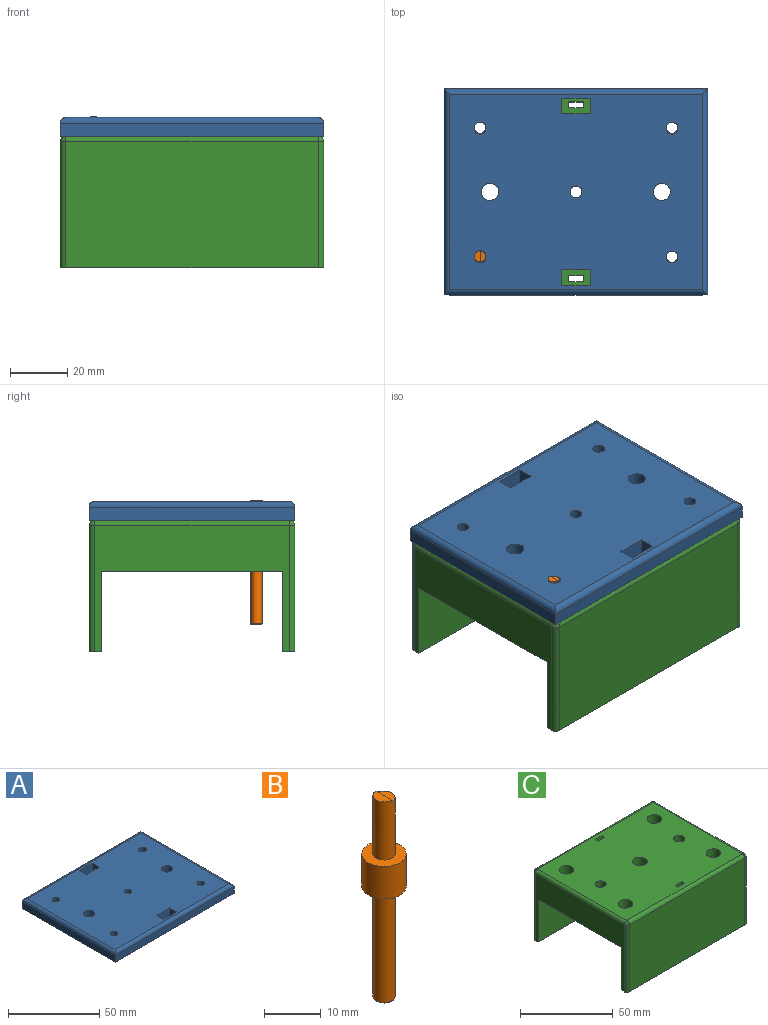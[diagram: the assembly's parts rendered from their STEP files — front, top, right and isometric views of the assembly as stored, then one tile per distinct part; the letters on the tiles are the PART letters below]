
ASSEMBLY  parts=3 mates=3
PART A: 35 faces, bbox 92x71.9x10.5 mm
  f0: plane 88x67.9mm, normal (0,0,1), area 5741mm2, adj f16,f17,f18,f19,f20,f21,f22,f23
  f1: plane 92x71.9mm, normal (0,0,-1), area 6201.9mm2, adj f2,f3,f4,f5,f6,f8,f10,f12
  f2: plane 71.9x4.5mm, normal (1,0,0), area 323.6mm2, adj f1,f3,f5,f21
  f3: plane 92x4.5mm, normal (0,1,0), area 414mm2, adj f1,f2,f4,f22
  f4: plane 71.9x4.5mm, normal (-1,0,0), area 323.6mm2, adj f1,f3,f5,f24
  f5: plane 92x4.5mm, normal (0,-1,0), area 414mm2, adj f1,f2,f4,f23
  f6: cylinder r=3.96mm len=7.92mm, axis (0,0,1), area 99.5mm2, adj f1,f7
  f7: plane 7.92x7.92mm, normal (0,0,-1), area 35.7mm2, adj f6,f20
  f8: cylinder r=3.96mm len=7.92mm, axis (0,0,1), area 99.5mm2, adj f1,f9
  f9: plane 7.92x7.92mm, normal (0,0,-1), area 35.7mm2, adj f8,f19
  f10: cylinder r=3.96mm len=7.92mm, axis (0,0,1), area 99.5mm2, adj f1,f11
  f11: plane 7.92x7.92mm, normal (0,0,-1), area 35.7mm2, adj f10,f18
  f12: cylinder r=3.96mm len=7.92mm, axis (0,0,1), area 99.5mm2, adj f1,f13
  f13: plane 7.92x7.92mm, normal (0,0,-1), area 35.7mm2, adj f12,f17
  f14: cylinder r=3.96mm len=7.92mm, axis (0,0,1), area 99.5mm2, adj f1,f15
  f15: plane 7.92x7.92mm, normal (0,0,-1), area 35.7mm2, adj f14,f16
  f16: cylinder r=2.08mm len=10.5mm, axis (0,0,1), area 136.9mm2, adj f0,f15
  f17: cylinder r=2.08mm len=10.5mm, axis (0,0,1), area 136.9mm2, adj f0,f13
  f18: cylinder r=2.08mm len=10.5mm, axis (0,0,1), area 136.9mm2, adj f0,f11
  f19: cylinder r=2.08mm len=10.5mm, axis (0,0,1), area 136.9mm2, adj f0,f9
  f20: cylinder r=2.08mm len=10.5mm, axis (0,0,1), area 136.9mm2, adj f0,f7
  f21: cylinder r=2mm len=71.9mm, axis (0,-1,0), area 221.3mm2, adj f0,f2,f22,f23
  f22: cylinder r=2mm len=92mm, axis (1,0,0), area 284.5mm2, adj f0,f3,f21,f24
  f23: cylinder r=2mm len=92mm, axis (-1,0,0), area 284.5mm2, adj f0,f5,f21,f24
  f24: cylinder r=2mm len=71.9mm, axis (0,1,0), area 221.3mm2, adj f0,f4,f22,f23
  f25: plane 6.5x5.5mm, normal (-1,0,0), area 35.8mm2, adj f0,f1,f26,f28
  f26: plane 10x6.5mm, normal (0,-1,0), area 65mm2, adj f0,f1,f25,f27
  f27: plane 6.5x5.5mm, normal (1,0,0), area 35.8mm2, adj f0,f1,f26,f28
  f28: plane 10x6.5mm, normal (0,1,0), area 65mm2, adj f0,f1,f25,f27
  f29: plane 10x6.5mm, normal (0,1,0), area 65mm2, adj f0,f1,f30,f32
  f30: plane 6.5x5.5mm, normal (-1,0,0), area 35.8mm2, adj f0,f1,f29,f31
  f31: plane 10x6.5mm, normal (0,-1,0), area 65mm2, adj f0,f1,f30,f32
  f32: plane 6.5x5.5mm, normal (1,0,0), area 35.8mm2, adj f0,f1,f29,f31
  f33: cylinder r=3mm len=6.5mm, axis (0,0,1), area 122.5mm2, adj f0,f1
  f34: cylinder r=3mm len=6.5mm, axis (0,0,1), area 122.5mm2, adj f0,f1
PART B: 10 faces, bbox 7.8x7.8x43.3 mm
  f0: cylinder r=3.9mm len=7.8mm, axis (0,0,1), area 171.5mm2, adj f1,f2
  f1: plane 7.8x7.8mm, normal (0,0,-1), area 35.8mm2, adj f0,f5
  f2: plane 7.8x7.8mm, normal (0,0,1), area 35.8mm2, adj f0,f3
  f3: cylinder r=1.95mm len=12.5mm, axis (0,0,-1), area 150.5mm2, adj f2,f4,f7,f8
  f4: plane 3.9x1.97mm, normal (0,0,1), area 6mm2, adj f3,f7
  f5: cylinder r=1.95mm len=23.63mm, axis (0,0,1), area 289.5mm2, adj f1,f9
  f6: plane 3.5x3.5mm, normal (0,0,-1), area 9.6mm2, adj f9
  f7: plane 3.9x0.43mm, normal (1,0,0), area 1.7mm2, adj f3,f4,f8
  f8: plane 3.91x1.96mm, normal (0,0,1), area 5.9mm2, adj f3,f7
  f9: torus R=1.75mm, axis (0,0,1), area 3.7mm2, adj f5,f6
PART C: 256 faces, bbox 92x71.9x46 mm
  f0: plane 67.9x44mm, normal (1,0,0), area 1122.2mm2, adj f6,f14,f15,f16,f17,f18,f21,f23
  f1: cylinder r=2.08mm len=4.15mm, axis (0,0,-1), area 52.2mm2, adj f6,f43
  f2: cylinder r=2.08mm len=4.15mm, axis (0,0,-1), area 52.2mm2, adj f6,f41
  f3: cylinder r=2.08mm len=4.15mm, axis (0,0,-1), area 52.2mm2, adj f6,f40
  f4: cylinder r=2.08mm len=4.15mm, axis (0,0,-1), area 52.2mm2, adj f6,f38
  f5: cylinder r=2.08mm len=4.15mm, axis (0,0,-1), area 52.2mm2, adj f6,f35
  f6: plane 92x63.4mm, normal (0,0,-1), area 5687.6mm2, adj f0,f1,f2,f3,f4,f5,f8,f15
  f7: plane 88x67.9mm, normal (0,0,1), area 5646.3mm2, adj f11,f12,f13,f14,f27,f28,f29,f30
  f8: plane 67.9x44mm, normal (-1,0,0), area 1212.4mm2, adj f6,f11,f15,f16,f17,f18,f19,f25
  f9: plane 88x44mm, normal (0,-1,0), area 3872mm2, adj f12,f16,f19,f21
  f10: plane 88x44mm, normal (0,1,0), area 3872mm2, adj f13,f18,f23,f25
  f11: cylinder r=2mm len=67.9mm, axis (0,-1,0), area 213.3mm2, adj f7,f8,f20,f26
  f12: cylinder r=2mm len=88mm, axis (1,0,0), area 276.5mm2, adj f7,f9,f20,f22
  f13: cylinder r=2mm len=88mm, axis (-1,0,0), area 276.5mm2, adj f7,f10,f24,f26
  f14: cylinder r=2mm len=67.9mm, axis (0,1,0), area 213.3mm2, adj f0,f7,f22,f24
  f15: plane 92x28mm, normal (0,1,0), area 2576mm2, adj f0,f6,f8,f16
  f16: plane 92x4.25mm, normal (0,0,-1), area 389.3mm2, adj f0,f8,f9,f15,f19,f21
  f17: plane 92x28mm, normal (0,-1,0), area 2576mm2, adj f0,f6,f8,f18
  f18: plane 92x4.25mm, normal (0,0,-1), area 389.3mm2, adj f0,f8,f10,f17,f23,f25
  f19: cylinder r=2mm len=44mm, axis (0,0,-1), area 138.2mm2, adj f8,f9,f16,f20
  f20: sphere r=2mm, area 6.3mm2, adj f11,f12,f19
  f21: cylinder r=2mm len=44mm, axis (0,0,1), area 138.2mm2, adj f0,f9,f16,f22
  f22: sphere r=2mm, area 6.3mm2, adj f12,f14,f21
  f23: cylinder r=2mm len=44mm, axis (0,0,-1), area 138.2mm2, adj f0,f10,f18,f24
  f24: sphere r=2mm, area 6.3mm2, adj f13,f14,f23
  f25: cylinder r=2mm len=44mm, axis (0,0,1), area 138.2mm2, adj f8,f10,f18,f26
  f26: sphere r=2mm, area 6.3mm2, adj f11,f13,f25
  f27: plane 18x5mm, normal (0,1,0), area 90mm2, adj f6,f7,f28,f30
  f28: plane 18x2.1mm, normal (1,0,0), area 37.8mm2, adj f6,f7,f27,f29
  f29: plane 18x5mm, normal (0,-1,0), area 90mm2, adj f6,f7,f28,f30
  f30: plane 18x2.1mm, normal (-1,0,0), area 37.8mm2, adj f6,f7,f27,f29
  f31: plane 18x5mm, normal (0,1,0), area 90mm2, adj f6,f7,f32,f34
  f32: plane 18x2.1mm, normal (1,0,0), area 37.8mm2, adj f6,f7,f31,f33
  f33: plane 18x5mm, normal (0,-1,0), area 90mm2, adj f6,f7,f32,f34
  f34: plane 18x2.1mm, normal (-1,0,0), area 37.8mm2, adj f6,f7,f31,f33
  f35: plane 8x8mm, normal (0,0,1), area 36.7mm2, adj f5,f36
  f36: cylinder r=4mm len=14mm, axis (0,0,1), area 351.9mm2, adj f7,f35
  f37: cylinder r=4mm len=14mm, axis (0,0,1), area 351.9mm2, adj f7,f38
  f38: plane 8x8mm, normal (0,0,1), area 36.7mm2, adj f4,f37
  f39: cylinder r=4mm len=14mm, axis (0,0,1), area 351.9mm2, adj f7,f40
  f40: plane 8x8mm, normal (0,0,1), area 36.7mm2, adj f3,f39
  f41: plane 8x8mm, normal (0,0,1), area 36.7mm2, adj f2,f42
  f42: cylinder r=4mm len=14mm, axis (0,0,1), area 351.9mm2, adj f7,f41
  f43: plane 8x8mm, normal (0,0,1), area 36.7mm2, adj f1,f44
  f44: cylinder r=4mm len=14mm, axis (0,0,1), area 351.9mm2, adj f7,f43
  f45: cylinder r=3mm len=18mm, axis (0,0,1), area 339.3mm2, adj f6,f7
  f46: cylinder r=3mm len=18mm, axis (0,0,1), area 339.3mm2, adj f6,f7
  f47: plane 1.1x0.56mm, normal (0,0,1), area 0.6mm2, adj f0,f48,f55,f56
  f48: plane 5.01x1.1mm, normal (0,-1,0), area 5.5mm2, adj f0,f47,f49,f56
  f49: plane 1.1x0.48mm, normal (0,0,-1), area 0.5mm2, adj f0,f48,f50,f56
  f50: plane 1.33x1.1mm, normal (0,0.61,-0.79), area 1.8mm2, adj f0,f49,f51,f56
  f51: plane 1.1x0.39mm, normal (0,0.79,0.61), area 0.5mm2, adj f0,f50,f52,f56
  f52: extruded ~1.1x0.82mm, area 1.2mm2, adj f0,f51,f53,f56
  f53: extruded ~1.1x0.16mm, area 0.2mm2, adj f0,f52,f54,f56
  f54: extruded ~1.1x0.84mm, area 0.9mm2, adj f0,f53,f55,f56
  f55: plane 3.57x1.1mm, normal (0,1,0), area 3.9mm2, adj f0,f47,f54,f56
  f56: plane 5.01x1.81mm, normal (1,0,0), area 3.4mm2, adj f47,f48,f49,f50,f51,f52,f53,f54
  f57: extruded ~1.25x1.1mm, area 1.5mm2, adj f0,f58,f75,f76
  f58: extruded ~1.1x0.79mm, area 0.9mm2, adj f0,f57,f59,f76
  f59: plane 1.51x1.1mm, normal (0,-1,0.08), area 1.7mm2, adj f0,f58,f60,f76
  f60: plane 2.01x1.1mm, normal (0,0,1), area 2.2mm2, adj f0,f59,f61,f76
  f61: plane 1.1x0.52mm, normal (0,-1,0), area 0.6mm2, adj f0,f60,f62,f76
  f62: plane 2.49x1.1mm, normal (0,0,-1), area 2.7mm2, adj f0,f61,f63,f76
  f63: plane 2.35x1.1mm, normal (0,1,-0.08), area 2.6mm2, adj f0,f62,f64,f76
  f64: plane 1.1x0.3mm, normal (0,0.54,0.84), area 0.4mm2, adj f0,f63,f65,f76
  f65: extruded ~1.1x0.87mm, area 1mm2, adj f0,f64,f66,f76
  f66: extruded ~1.28x1.1mm, area 2.1mm2, adj f0,f65,f67,f76
  f67: extruded ~1.1x0.82mm, area 1mm2, adj f0,f66,f68,f76
  f68: extruded ~1.1x0.94mm, area 1.1mm2, adj f0,f67,f69,f76
  f69: extruded ~1.1x0.7mm, area 0.8mm2, adj f0,f68,f70,f76
  f70: extruded ~1.1x0.6mm, area 0.7mm2, adj f0,f69,f71,f76
  f71: plane 1.1x0.55mm, normal (0,1,0), area 0.6mm2, adj f0,f70,f72,f76
  f72: extruded ~1.29x1.1mm, area 1.5mm2, adj f0,f71,f73,f76
  f73: extruded ~1.37x1.1mm, area 1.6mm2, adj f0,f72,f74,f76
  f74: extruded ~1.22x1.1mm, area 1.5mm2, adj f0,f73,f75,f76
  f75: extruded ~1.1x1.08mm, area 1.3mm2, adj f0,f57,f74,f76
  f76: plane 5.08x3.15mm, normal (1,0,0), area 5.8mm2, adj f57,f58,f59,f60,f61,f62,f63,f64
  f77: extruded ~1.1x0.79mm, area 0.9mm2, adj f0,f78,f104,f105
  f78: extruded ~1.1x0.92mm, area 1.1mm2, adj f0,f77,f79,f105
  f79: extruded ~1.13x1.1mm, area 1.3mm2, adj f0,f78,f80,f105
  f80: extruded ~1.1x0.85mm, area 1mm2, adj f0,f79,f81,f105
  f81: extruded ~1.1x0.71mm, area 0.9mm2, adj f0,f80,f82,f105
  f82: plane 1.1x0.38mm, normal (0,0.8,0.6), area 0.5mm2, adj f0,f81,f83,f105
  f83: extruded ~1.1x0.67mm, area 0.8mm2, adj f0,f82,f84,f105
  f84: extruded ~1.1x0.62mm, area 0.7mm2, adj f0,f83,f85,f105
  f85: extruded ~1.1x0.68mm, area 0.8mm2, adj f0,f84,f86,f105
  f86: extruded ~1.1x0.58mm, area 0.7mm2, adj f0,f85,f87,f105
  f87: extruded ~1.1x0.72mm, area 0.9mm2, adj f0,f86,f88,f105
  f88: extruded ~1.1x0.93mm, area 1.1mm2, adj f0,f87,f89,f105
  f89: plane 1.1x0.5mm, normal (0,0,-1), area 0.6mm2, adj f0,f88,f90,f105
  f90: plane 1.1x0.49mm, normal (0,1,0), area 0.5mm2, adj f0,f89,f91,f105
  f91: plane 1.1x0.49mm, normal (0,0,1), area 0.5mm2, adj f0,f90,f92,f105
  f92: extruded ~1.43x1.1mm, area 2.1mm2, adj f0,f91,f93,f105
  f93: extruded ~1.3x1.1mm, area 2.1mm2, adj f0,f92,f94,f105
  f94: extruded ~1.1x0.7mm, area 0.8mm2, adj f0,f93,f95,f105
  f95: extruded ~1.1x0.69mm, area 0.8mm2, adj f0,f94,f96,f105
  f96: plane 1.1x0.54mm, normal (0,1,0), area 0.6mm2, adj f0,f95,f97,f105
  f97: extruded ~1.1x0.64mm, area 0.7mm2, adj f0,f96,f98,f105
  f98: extruded ~1.1x0.73mm, area 0.8mm2, adj f0,f97,f99,f105
  f99: extruded ~1.41x1.1mm, area 1.6mm2, adj f0,f98,f100,f105
  f100: extruded ~1.1x1.1mm, area 1.4mm2, adj f0,f99,f101,f105
  f101: extruded ~1.1x0.81mm, area 1mm2, adj f0,f100,f102,f105
  f102: extruded ~1.1x0.89mm, area 1.1mm2, adj f0,f101,f103,f105
  f103: plane 1.1x0.03mm, normal (0,-1,0), area 0mm2, adj f0,f102,f104,f105
  f104: extruded ~1.1x0.76mm, area 1mm2, adj f0,f77,f103,f105
  f105: plane 5.15x3.28mm, normal (1,0,0), area 5.8mm2, adj f77,f78,f79,f80,f81,f82,f83,f84
  f106: extruded ~1.59x1.1mm, area 1.8mm2, adj f107,f121,f122,f251
  f107: extruded ~1.59x1.1mm, area 1.8mm2, adj f106,f108,f122,f251
  f108: extruded ~1.1x0.82mm, area 1.1mm2, adj f107,f109,f122,f251
  f109: extruded ~1.1x0.82mm, area 1.1mm2, adj f108,f110,f122,f251
  f110: extruded ~1.58x1.1mm, area 1.8mm2, adj f109,f111,f122,f251
  f111: extruded ~1.59x1.1mm, area 1.8mm2, adj f110,f112,f122,f251
  f112: extruded ~1.1x0.82mm, area 1.1mm2, adj f111,f121,f122,f251
  f113: extruded ~1.94x1.1mm, area 2.2mm2, adj f0,f114,f120,f122
  f114: extruded ~1.92x1.1mm, area 2.2mm2, adj f0,f113,f115,f122
  f115: extruded ~1.24x1.1mm, area 1.6mm2, adj f0,f114,f116,f122
  f116: extruded ~1.24x1.1mm, area 1.6mm2, adj f0,f115,f117,f122
  f117: extruded ~1.94x1.1mm, area 2.2mm2, adj f0,f116,f118,f122
  f118: extruded ~1.93x1.1mm, area 2.2mm2, adj f0,f117,f119,f122
  f119: extruded ~1.23x1.1mm, area 1.6mm2, adj f0,f118,f120,f122
  f120: extruded ~1.25x1.1mm, area 1.6mm2, adj f0,f113,f119,f122
  f121: extruded ~1.1x0.82mm, area 1.1mm2, adj f106,f112,f122,f251
  f122: plane 5.16x3.31mm, normal (1,0,0), area 6.6mm2, adj f106,f107,f108,f109,f110,f111,f112,f113
  f123: plane 3.17x1.1mm, normal (0,0,1), area 3.5mm2, adj f0,f124,f126,f127
  f124: plane 1.1x0.45mm, normal (0,-1,0), area 0.5mm2, adj f0,f123,f125,f127
  f125: plane 3.17x1.1mm, normal (0,0,-1), area 3.5mm2, adj f0,f124,f126,f127
  f126: plane 1.1x0.45mm, normal (0,1,0), area 0.5mm2, adj f0,f123,f125,f127
  f127: plane 3.17x0.45mm, normal (1,0,0), area 1.4mm2, adj f123,f124,f125,f126
  f128: plane 1.1x0.52mm, normal (0,1,0), area 0.6mm2, adj f0,f129,f131,f132
  f129: plane 1.68x1.1mm, normal (0,0,1), area 1.9mm2, adj f0,f128,f130,f132
  f130: plane 1.1x0.52mm, normal (0,-1,0), area 0.6mm2, adj f0,f129,f131,f132
  f131: plane 1.68x1.1mm, normal (0,0,-1), area 1.9mm2, adj f0,f128,f130,f132
  f132: plane 1.68x0.52mm, normal (1,0,0), area 0.9mm2, adj f128,f129,f130,f131
  f133: plane 1.7x1.1mm, normal (0,0,-1), area 1.9mm2, adj f0,f134,f152,f153
  f134: plane 1.1x0.52mm, normal (0,1,0), area 0.6mm2, adj f0,f133,f135,f153
  f135: plane 1.12x1.1mm, normal (0,0,1), area 1.2mm2, adj f0,f134,f136,f153
  f136: plane 1.54x1.1mm, normal (0,1,0), area 1.7mm2, adj f0,f135,f137,f153
  f137: extruded ~1.1x1.02mm, area 1.1mm2, adj f0,f136,f138,f153
  f138: extruded ~1.46x1.1mm, area 1.8mm2, adj f0,f137,f139,f153
  f139: extruded ~1.54x1.1mm, area 1.8mm2, adj f0,f138,f140,f153
  f140: extruded ~1.51x1.1mm, area 1.8mm2, adj f0,f139,f141,f153
  f141: extruded ~1.43x1.1mm, area 1.7mm2, adj f0,f140,f142,f153
  f142: extruded ~1.31x1.1mm, area 1.5mm2, adj f0,f141,f143,f153
  f143: plane 1.1x0.51mm, normal (0,-0.92,0.4), area 0.6mm2, adj f0,f142,f144,f153
  f144: extruded ~1.5x1.1mm, area 1.7mm2, adj f0,f143,f145,f153
  f145: extruded ~1.38x1.1mm, area 1.6mm2, adj f0,f144,f146,f153
  f146: extruded ~1.1x0.9mm, area 1.4mm2, adj f0,f145,f147,f153
  f147: extruded ~1.37x1.1mm, area 1.6mm2, adj f0,f146,f148,f153
  f148: extruded ~1.9x1.1mm, area 2.3mm2, adj f0,f147,f149,f153
  f149: extruded ~1.77x1.1mm, area 2.1mm2, adj f0,f148,f150,f153
  f150: extruded ~1.1x0.95mm, area 1.1mm2, adj f0,f149,f151,f153
  f151: extruded ~1.1x0.81mm, area 0.9mm2, adj f0,f150,f152,f153
  f152: plane 2.44x1.1mm, normal (0,-1,0), area 2.7mm2, adj f0,f133,f151,f153
  f153: plane 5.15x4.17mm, normal (1,0,0), area 7.6mm2, adj f133,f134,f135,f136,f137,f138,f139,f140
  f154: plane 1.1x0.58mm, normal (0,0,1), area 0.6mm2, adj f0,f155,f163,f164
  f155: plane 2.14x1.1mm, normal (0,-1,0), area 2.4mm2, adj f0,f154,f156,f164
  f156: plane 2.08x1.1mm, normal (0,0,1), area 2.3mm2, adj f0,f155,f157,f164
  f157: plane 1.1x0.52mm, normal (0,-1,0), area 0.6mm2, adj f0,f156,f158,f164
  f158: plane 2.08x1.1mm, normal (0,0,-1), area 2.3mm2, adj f0,f157,f159,f164
  f159: plane 1.83x1.1mm, normal (0,-1,0), area 2mm2, adj f0,f158,f160,f164
  f160: plane 2.21x1.1mm, normal (0,0,1), area 2.4mm2, adj f0,f159,f161,f164
  f161: plane 1.1x0.52mm, normal (0,-1,0), area 0.6mm2, adj f0,f160,f162,f164
  f162: plane 2.79x1.1mm, normal (0,0,-1), area 3.1mm2, adj f0,f161,f163,f164
  f163: plane 5.01x1.1mm, normal (0,1,0), area 5.5mm2, adj f0,f154,f162,f164
  f164: plane 5.01x2.79mm, normal (1,0,0), area 5.1mm2, adj f154,f155,f156,f157,f158,f159,f160,f161
  f165: extruded ~1.59x1.1mm, area 1.8mm2, adj f166,f180,f181,f252
  f166: extruded ~1.59x1.1mm, area 1.8mm2, adj f165,f167,f181,f252
  f167: extruded ~1.1x0.82mm, area 1.1mm2, adj f166,f168,f181,f252
  f168: extruded ~1.1x0.82mm, area 1.1mm2, adj f167,f169,f181,f252
  f169: extruded ~1.58x1.1mm, area 1.8mm2, adj f168,f170,f181,f252
  f170: extruded ~1.59x1.1mm, area 1.8mm2, adj f169,f171,f181,f252
  f171: extruded ~1.1x0.82mm, area 1.1mm2, adj f170,f180,f181,f252
  f172: extruded ~1.94x1.1mm, area 2.2mm2, adj f0,f173,f179,f181
  f173: extruded ~1.92x1.1mm, area 2.2mm2, adj f0,f172,f174,f181
  f174: extruded ~1.24x1.1mm, area 1.6mm2, adj f0,f173,f175,f181
  f175: extruded ~1.24x1.1mm, area 1.6mm2, adj f0,f174,f176,f181
  f176: extruded ~1.94x1.1mm, area 2.2mm2, adj f0,f175,f177,f181
  f177: extruded ~1.93x1.1mm, area 2.2mm2, adj f0,f176,f178,f181
  f178: extruded ~1.23x1.1mm, area 1.6mm2, adj f0,f177,f179,f181
  f179: extruded ~1.25x1.1mm, area 1.6mm2, adj f0,f172,f178,f181
  f180: extruded ~1.1x0.82mm, area 1.1mm2, adj f165,f171,f181,f252
  f181: plane 5.16x3.31mm, normal (1,0,0), area 6.6mm2, adj f165,f166,f167,f168,f169,f170,f171,f172
  f182: plane 1.67x1.1mm, normal (0,1,0), area 1.8mm2, adj f183,f198,f199,f253
  f183: plane 1.87x1.1mm, normal (0,0,-1), area 2.1mm2, adj f182,f184,f199,f253
  f184: plane 2.23x1.57mm, normal (0,-0.82,0.58), area 3mm2, adj f183,f185,f199,f253
  f185: extruded ~1.1x0.55mm, area 0.7mm2, adj f184,f186,f199,f253
  f186: plane 1.1x0.03mm, normal (0,0,1), area 0mm2, adj f185,f198,f199,f253
  f187: plane 1.1x0.74mm, normal (0,0,1), area 0.8mm2, adj f0,f188,f197,f199
  f188: plane 1.1x0.52mm, normal (0,-1,0), area 0.6mm2, adj f0,f187,f189,f199
  f189: plane 1.1x0.74mm, normal (0,0,-1), area 0.8mm2, adj f0,f188,f190,f199
  f190: plane 3.37x1.1mm, normal (0,-1,0), area 3.7mm2, adj f0,f189,f191,f199
  f191: plane 1.1x0.6mm, normal (0,0,-1), area 0.7mm2, adj f0,f190,f192,f199
  f192: plane 3.39x2.38mm, normal (0,0.82,-0.57), area 4.6mm2, adj f0,f191,f193,f199
  f193: plane 1.1x0.5mm, normal (0,1,0), area 0.5mm2, adj f0,f192,f194,f199
  f194: plane 2.44x1.1mm, normal (0,0,1), area 2.7mm2, adj f0,f193,f195,f199
  f195: plane 1.15x1.1mm, normal (0,1,0), area 1.3mm2, adj f0,f194,f196,f199
  f196: plane 1.1x0.55mm, normal (0,0,1), area 0.6mm2, adj f0,f195,f197,f199
  f197: plane 1.15x1.1mm, normal (0,-1,0), area 1.3mm2, adj f0,f187,f196,f199
  f198: extruded ~1.11x1.1mm, area 1.2mm2, adj f182,f186,f199,f253
  f199: plane 5.04x3.73mm, normal (1,0,0), area 6.1mm2, adj f182,f183,f184,f185,f186,f187,f188,f189
  f200: plane 1.67x1.1mm, normal (0,1,0), area 1.8mm2, adj f201,f216,f217,f254
  f201: plane 1.87x1.1mm, normal (0,0,-1), area 2.1mm2, adj f200,f202,f217,f254
  f202: plane 2.23x1.57mm, normal (0,-0.82,0.58), area 3mm2, adj f201,f203,f217,f254
  f203: extruded ~1.1x0.55mm, area 0.7mm2, adj f202,f204,f217,f254
  f204: plane 1.1x0.03mm, normal (0,0,1), area 0mm2, adj f203,f216,f217,f254
  f205: plane 1.1x0.74mm, normal (0,0,1), area 0.8mm2, adj f0,f206,f215,f217
  f206: plane 1.1x0.52mm, normal (0,-1,0), area 0.6mm2, adj f0,f205,f207,f217
  f207: plane 1.1x0.74mm, normal (0,0,-1), area 0.8mm2, adj f0,f206,f208,f217
  f208: plane 3.37x1.1mm, normal (0,-1,0), area 3.7mm2, adj f0,f207,f209,f217
  f209: plane 1.1x0.6mm, normal (0,0,-1), area 0.7mm2, adj f0,f208,f210,f217
  f210: plane 3.39x2.38mm, normal (0,0.82,-0.57), area 4.6mm2, adj f0,f209,f211,f217
  f211: plane 1.1x0.5mm, normal (0,1,0), area 0.5mm2, adj f0,f210,f212,f217
  f212: plane 2.44x1.1mm, normal (0,0,1), area 2.7mm2, adj f0,f211,f213,f217
  f213: plane 1.15x1.1mm, normal (0,1,0), area 1.3mm2, adj f0,f212,f214,f217
  f214: plane 1.1x0.55mm, normal (0,0,1), area 0.6mm2, adj f0,f213,f215,f217
  f215: plane 1.15x1.1mm, normal (0,-1,0), area 1.3mm2, adj f0,f205,f214,f217
  f216: extruded ~1.11x1.1mm, area 1.2mm2, adj f200,f204,f217,f254
  f217: plane 5.04x3.73mm, normal (1,0,0), area 6.1mm2, adj f200,f201,f202,f203,f204,f205,f206,f207
  f218: extruded ~1.1x0.76mm, area 0.9mm2, adj f219,f242,f243,f255
  f219: extruded ~1.1x0.57mm, area 0.7mm2, adj f218,f220,f243,f255
  f220: extruded ~1.1x0.48mm, area 0.7mm2, adj f219,f221,f243,f255
  f221: extruded ~1.1x0.66mm, area 0.7mm2, adj f220,f222,f243,f255
  f222: extruded ~1.1x0.46mm, area 0.5mm2, adj f221,f223,f243,f255
  f223: extruded ~1.1x0.41mm, area 0.6mm2, adj f222,f224,f243,f255
  f224: extruded ~1.1x0.57mm, area 0.6mm2, adj f223,f225,f243,f255
  f225: extruded ~1.1x0.75mm, area 0.9mm2, adj f224,f226,f243,f255
  f226: extruded ~1.1x0.78mm, area 0.9mm2, adj f225,f242,f243,f255
  f227: extruded ~2.21x1.1mm, area 2.6mm2, adj f0,f228,f241,f243
  f228: extruded ~1.63x1.1mm, area 1.9mm2, adj f0,f227,f229,f243
  f229: extruded ~1.23x1.1mm, area 1.6mm2, adj f0,f228,f230,f243
  f230: extruded ~1.15x1.1mm, area 1.4mm2, adj f0,f229,f231,f243
  f231: extruded ~1.23x1.1mm, area 1.5mm2, adj f0,f230,f232,f243
  f232: extruded ~1.11x1.1mm, area 1.3mm2, adj f0,f231,f233,f243
  f233: extruded ~1.1x1.06mm, area 1.3mm2, adj f0,f232,f234,f243
  f234: extruded ~1.19x1.1mm, area 1.5mm2, adj f0,f233,f235,f243
  f235: plane 1.1x0.04mm, normal (0,0,-1), area 0mm2, adj f0,f234,f236,f243
  f236: extruded ~1.58x1.1mm, area 1.8mm2, adj f0,f235,f237,f243
  f237: extruded ~1.23x1.1mm, area 1.5mm2, adj f0,f236,f238,f243
  f238: extruded ~1.1x0.6mm, area 0.7mm2, adj f0,f237,f239,f243
  f239: plane 1.1x0.49mm, normal (0,-1,0), area 0.5mm2, adj f0,f238,f240,f243
  f240: extruded ~1.1x0.61mm, area 0.7mm2, adj f0,f239,f241,f243
  f241: extruded ~1.7x1.1mm, area 2.1mm2, adj f0,f227,f240,f243
  f242: extruded ~1.1x0.89mm, area 1mm2, adj f218,f226,f243,f255
  f243: plane 5.15x3.27mm, normal (1,0,0), area 6.5mm2, adj f218,f219,f220,f221,f222,f223,f224,f225
  f244: plane 5.01x1.1mm, normal (0,1,0), area 5.5mm2, adj f0,f245,f249,f250
  f245: plane 2.79x1.1mm, normal (0,0,1), area 3.1mm2, adj f0,f244,f246,f250
  f246: plane 1.1x0.53mm, normal (0,-1,0), area 0.6mm2, adj f0,f245,f247,f250
  f247: plane 2.21x1.1mm, normal (0,0,-1), area 2.4mm2, adj f0,f246,f248,f250
  f248: plane 4.48x1.1mm, normal (0,-1,0), area 4.9mm2, adj f0,f247,f249,f250
  f249: plane 1.1x0.58mm, normal (0,0,-1), area 0.6mm2, adj f0,f244,f248,f250
  f250: plane 5.01x2.79mm, normal (1,0,0), area 4.1mm2, adj f244,f245,f246,f247,f248,f249
  f251: plane 4.18x2.16mm, normal (1,0,0), area 7.6mm2, adj f106,f107,f108,f109,f110,f111,f112,f121
  f252: plane 4.18x2.16mm, normal (1,0,0), area 7.6mm2, adj f165,f166,f167,f168,f169,f170,f171,f180
  f253: plane 2.77x1.9mm, normal (1,0,0), area 2.5mm2, adj f182,f183,f184,f185,f186,f198
  f254: plane 2.77x1.9mm, normal (1,0,0), area 2.5mm2, adj f200,f201,f202,f203,f204,f216
  f255: plane 2.26x2.12mm, normal (1,0,0), area 3.9mm2, adj f218,f219,f220,f221,f222,f223,f224,f225
PLACE A t=(52.61,19.3,7)mm
PLACE B t=(19.11,-3.2,1.42)mm
PLACE C t=(52.61,19.3,7)mm
MATE slider B.f0 <-> C.f3  axis (0,0,-1) through (19.11,-3.2,-5.58)mm
MATE planar B.f8 <-> A.f20  axis (0,0,1) through (21.06,-3.2,13.5)mm
MATE fastened C.f36 <-> A.f6  axis (0,0,1) through (52.61,19.3,7)mm
